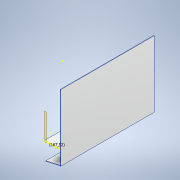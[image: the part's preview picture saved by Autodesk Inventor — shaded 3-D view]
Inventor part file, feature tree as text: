
AUTODESK INVENTOR PART (.ipt)
format: ipt  version: 2022.3 (Build 263350000, 350)  size: 151,040 bytes
history: native  units: mm
features: reference x15, other x6, sketch x3, extrude x2, projected_geometry x2, plane x1
ambient origin geometry x8: Origin, YZ Plane, XZ Plane, XY Plane, X Axis, Y Axis, Z Axis, Center Point
bodies: Solid1 (feature_tree)
feature tree (29):
  extrude  "Extrusion1"  Depth=0.5mm
  plane  "Work Plane1"
  extrude  "Extrusion2"  Depth=0.5mm
  sketch  "Sketch3"  dims[d6=100.0mm d7=0.0mm d8=0.5mm d9=60.0mm d10=0.0mm d11=29.238253mm]
  sketch  "Sketch1"  dims[d0=0.5mm d1=0.5mm]
  reference  "Reference1"
  reference  "Reference2"
  reference  "Reference3"
  reference  "Reference4"
  reference  "Reference5"
  reference  "Reference6"
  reference  "Reference7"
  reference  "Reference8"
  reference  "Reference9"
  reference  "Reference10"
  reference  "Reference11"
  sketch  "Sketch2"  dims[d4=0.5mm d5=0.5mm]
  reference  "Reference12"
  reference  "Reference13"
  reference  "Reference14"
  reference  "Reference15"
  projected_geometry  "Projected Loop1"
  projected_geometry  "Projected Loop2"
  other  "Assembly2"
  other  "pług:1"
  other  "sciana_lewa_v3:1"
  other  "minisumopodsr:1"
  other  "uchwytlewy:1"
  other  "uchwytprawy:1"
